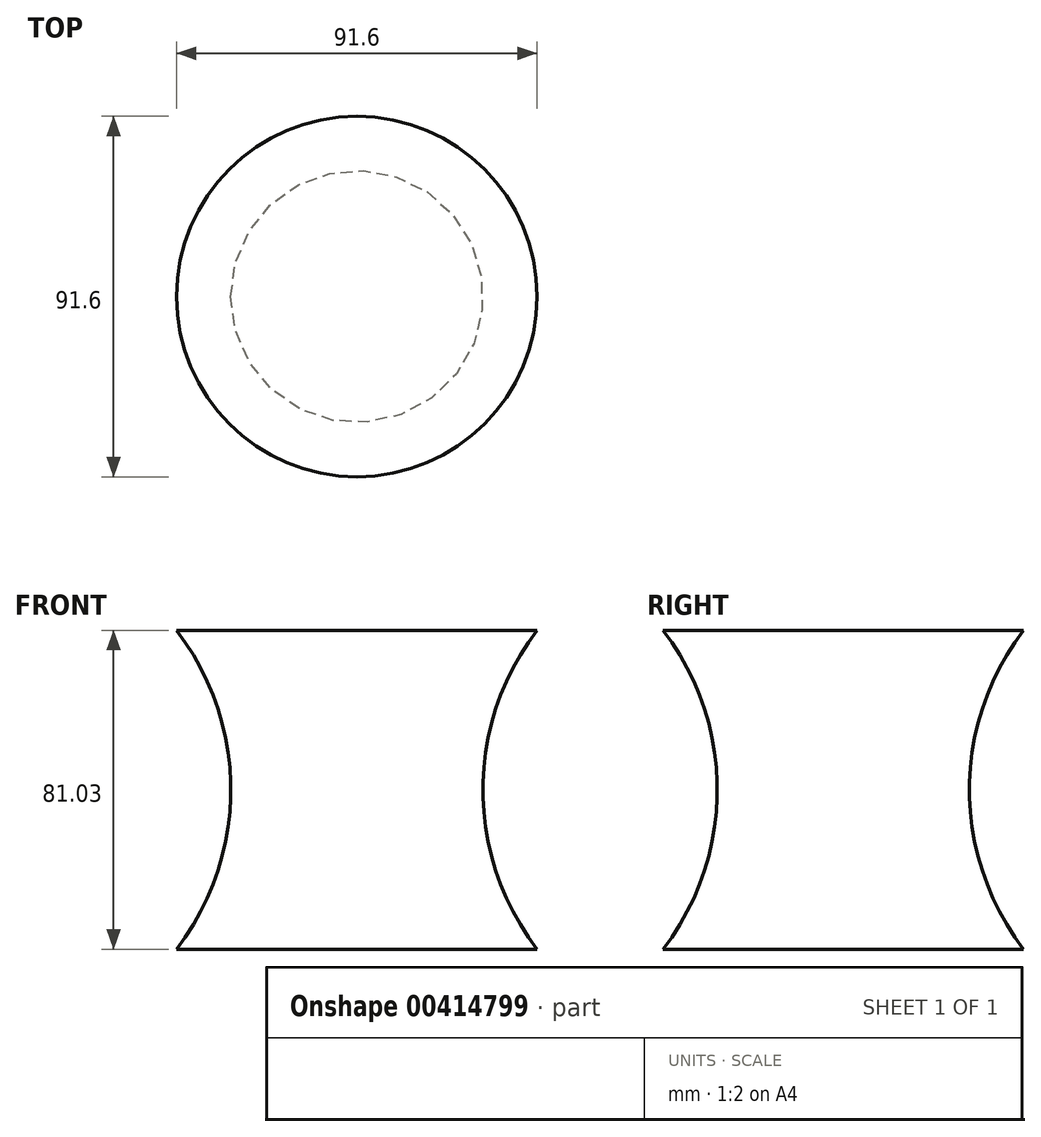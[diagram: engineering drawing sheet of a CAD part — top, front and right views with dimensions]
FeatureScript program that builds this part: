
annotation { "Feature Type Name" : "Feature", "Feature Type Description" : "" }
export const myFeature = defineFeature(function(context is Context, id is Id, definition is map)
    precondition{}
    {
        {
            var Q0;
            Q0=qCreatedBy(makeId("Top.planeOp"),FACE);
            var sketch = newSketch(context, id + "F0", { "sketchPlane" : qUnion([Q0])});
            skCircle(sketch, "E0", {"center": v(0, 0) * mm, "radius": 25 * mm});
            skSolve(sketch);
        }
        {
            var Q0;
            Q0=qCreatedBy(makeId("Top.planeOp"),FACE);
            var sketch = newSketch(context, id + "F1", { "sketchPlane" : qUnion([Q0])});
            skCircle(sketch, "E1", {"center": v(0, 0) * mm, "radius": 45.8 * mm});
            skSolve(sketch);
        }
        {
            var Q0;
            Q0=qCreatedBy(makeId("Front.planeOp"),FACE);
            var sketch = newSketch(context, id + "F2", { "sketchPlane" : qUnion([Q0])});
            skArc(sketch, "E2", {"start": v(-45.8, 0) * mm, "mid": v(-32.03, 40.52) * mm, "end": v(-45.8, 81.03) * mm});
            skLineSegment(sketch, "E3", {"start": v(-45.8, 81.03) * mm, "end": v(0, 81.03) * mm});
            skLineSegment(sketch, "E4", {"start": v(-45.8, 0) * mm, "end": v(45.8, 0) * mm});
            skLineSegment(sketch, "E5", {"start": v(-45.8, 0) * mm, "end": v(0, 0) * mm});
            skLineSegment(sketch, "E6", {"start": v(0, 0) * mm, "end": v(0, 81.03) * mm});
            skSolve(sketch);
        }
        {
            var Q0;
            Q0=makeQuery(id+"F2.imprint","IMPRINT",FACE,{"disambiguationData":[TD([[makeQuery(id+"F2.imprint","IMPRINT",EDGE,{"derivedFrom":sQuery(id+"F2.wireOp",EDGE,"E2")}),-1.0]])]});
            var Q1;
            Q1=sQuery(id+"F2.wireOp",EDGE,"E6");
            revolve(context, id + "F3", {"entities" : qUnion([Q0]), "axis" : qUnion([Q1]), "revolveType" : RevolveType.FULL});
        }
    });
